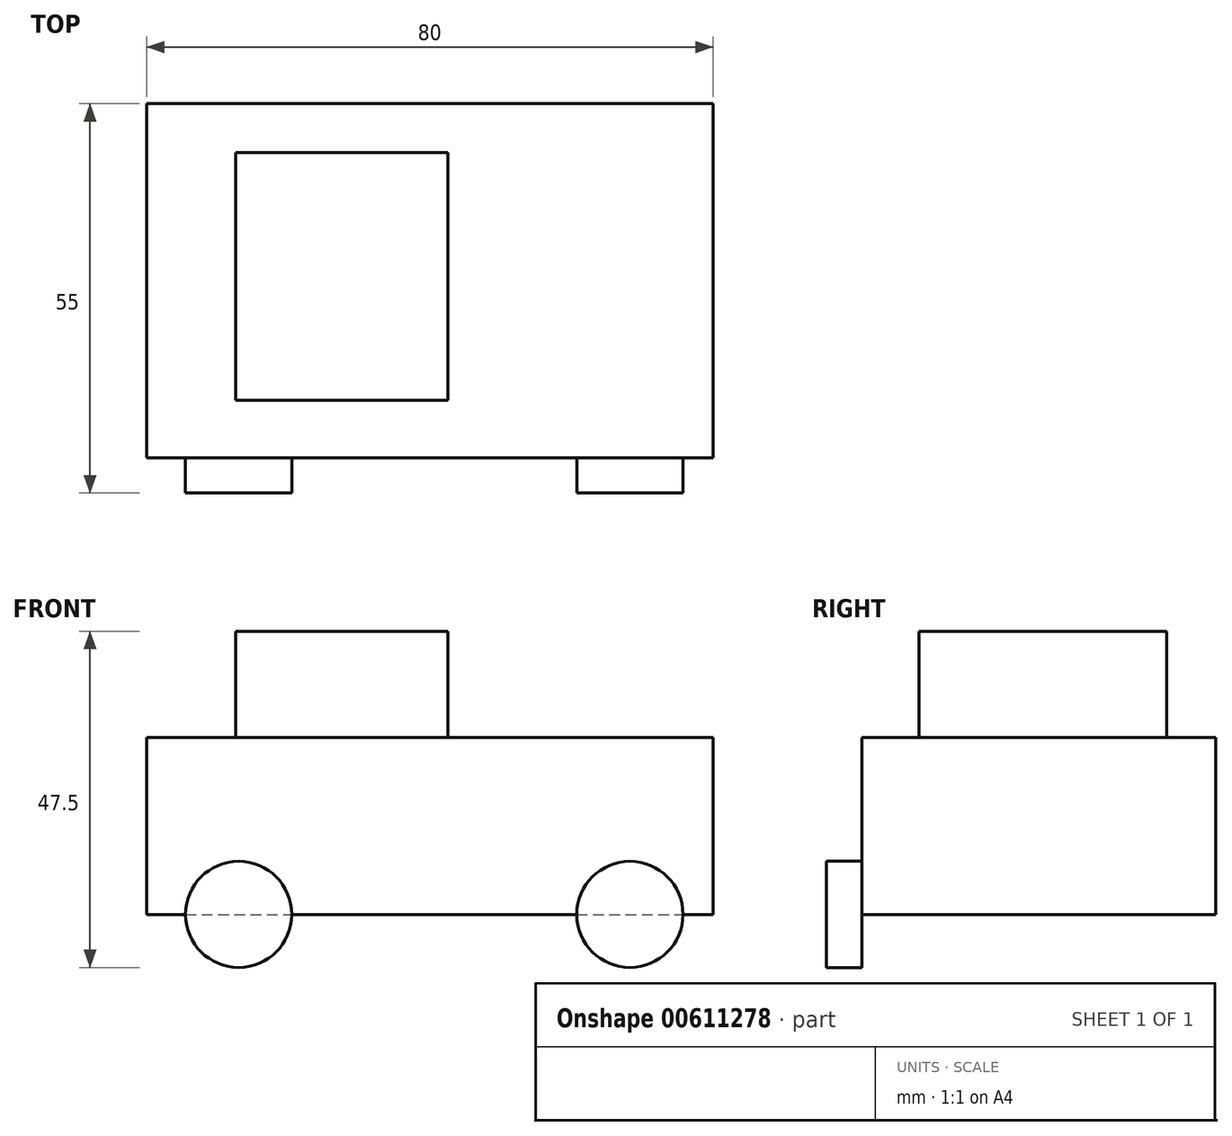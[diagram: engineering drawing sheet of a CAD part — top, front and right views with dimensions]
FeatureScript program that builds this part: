
annotation { "Feature Type Name" : "Feature", "Feature Type Description" : "" }
export const myFeature = defineFeature(function(context is Context, id is Id, definition is map)
    precondition{}
    {
        {
            var Q0;
            Q0=qCreatedBy(makeId("Top.planeOp"),FACE);
            var sketch = newSketch(context, id + "F0", { "sketchPlane" : qUnion([Q0])});
            skLineSegment(sketch, "E0.bottom", {"start": v(-39.37, 0) * mm, "end": v(40.63, 0) * mm});
            skLineSegment(sketch, "E0.top", {"start": v(-39.37, -50) * mm, "end": v(40.63, -50) * mm});
            skLineSegment(sketch, "E0.left", {"start": v(-39.37, 0) * mm, "end": v(-39.37, -50) * mm});
            skLineSegment(sketch, "E0.right", {"start": v(40.63, 0) * mm, "end": v(40.63, -50) * mm});
            skSolve(sketch);
        }
        {
            var Q0;
            Q0=makeQuery(id+"F0.imprint","IMPRINT",FACE,{"disambiguationData":[TD([[makeQuery(id+"F0.imprint","IMPRINT",EDGE,{"derivedFrom":sQuery(id+"F0.wireOp",EDGE,"E0.bottom")}),-1.0]])]});
            extrude(context, id + "F1", {"entities" : qUnion([Q0]), "depth" : 25 * mm, "offsetDistance" : 25 * mm});
        }
        {
            var Q0;
            Q0=makeQuery(id+"F1.opExtrude","CAP_FACE",FACE,{"disambiguationData":[OSD([sQuery(id+"F0.wireOp",EDGE,"E0.bottom"),sQuery(id+"F0.wireOp",EDGE,"E0.top"),sQuery(id+"F0.wireOp",EDGE,"E0.left"),sQuery(id+"F0.wireOp",EDGE,"E0.right")])],"isStart":false});
            var sketch = newSketch(context, id + "F2", { "sketchPlane" : qUnion([Q0])});
            skLineSegment(sketch, "E1.bottom", {"start": v(-26.8, -41.9) * mm, "end": v(3.2, -41.9) * mm});
            skLineSegment(sketch, "E1.top", {"start": v(-26.8, -6.9) * mm, "end": v(3.2, -6.9) * mm});
            skLineSegment(sketch, "E1.left", {"start": v(-26.8, -41.9) * mm, "end": v(-26.8, -6.9) * mm});
            skLineSegment(sketch, "E1.right", {"start": v(3.2, -41.9) * mm, "end": v(3.2, -6.9) * mm});
            skSolve(sketch);
        }
        {
            var Q0;
            Q0=makeQuery(id+"F2.imprint","IMPRINT",FACE,{"disambiguationData":[TD([[makeQuery(id+"F2.imprint","IMPRINT",EDGE,{"derivedFrom":sQuery(id+"F2.wireOp",EDGE,"E1.bottom")}),1.0]])]});
            extrude(context, id + "F3", {"entities" : qUnion([Q0]), "operationType" : NewBodyOperationType.ADD, "depth" : 15 * mm, "offsetDistance" : 25 * mm});
        }
        {
            var Q0;
            Q0=makeQuery(id+"F1.opExtrude","SWEPT_FACE",FACE,{"disambiguationData":[OSD([sQuery(id+"F0.wireOp",EDGE,"E0.top")])]});
            var sketch = newSketch(context, id + "F4", { "sketchPlane" : qUnion([Q0])});
            skCircle(sketch, "E2", {"center": v(-26.38, 0) * mm, "radius": 7.5 * mm});
            skCircle(sketch, "E3", {"center": v(28.88, 0) * mm, "radius": 7.5 * mm});
            skSolve(sketch);
        }
        {
            var Q0;
            {var subQ0=sQuery(id+"F4.wireOp",EDGE,"E2");var subQ1=makeQuery(id+"F1.opExtrude","CAP_EDGE",EDGE,{"disambiguationData":[OSD([sQuery(id+"F0.wireOp",EDGE,"E0.top")])],"isStart":true});var subQ2=makeQuery(id+"F4.imprint","INTERSECT",VERTEX,{"disambiguationData":[OD(0.0)],"derivedFrom":[subQ1,subQ0]});Q0=makeQuery(id+"F4.imprint","IMPRINT",FACE,{"disambiguationData":[TD([[makeQuery(id+"F4.imprint","IMPRINT",EDGE,{"disambiguationData":[TD([[subQ2,-1.0]])],"derivedFrom":subQ0}),1.0]])]});}
            var Q1;
            {var subQ0=sQuery(id+"F4.wireOp",EDGE,"E3");var subQ1=makeQuery(id+"F1.opExtrude","CAP_EDGE",EDGE,{"disambiguationData":[OSD([sQuery(id+"F0.wireOp",EDGE,"E0.top")])],"isStart":true});var subQ2=makeQuery(id+"F4.imprint","INTERSECT",VERTEX,{"disambiguationData":[OD(0.0)],"derivedFrom":[subQ1,subQ0]});Q1=makeQuery(id+"F4.imprint","IMPRINT",FACE,{"disambiguationData":[TD([[makeQuery(id+"F4.imprint","IMPRINT",EDGE,{"disambiguationData":[TD([[subQ2,1.0]])],"derivedFrom":subQ0}),1.0]])]});}
            var Q2;
            {var subQ0=sQuery(id+"F4.wireOp",EDGE,"E2");var subQ1=makeQuery(id+"F1.opExtrude","CAP_EDGE",EDGE,{"disambiguationData":[OSD([sQuery(id+"F0.wireOp",EDGE,"E0.top")])],"isStart":true});var subQ2=makeQuery(id+"F4.imprint","INTERSECT",VERTEX,{"disambiguationData":[OD(0.0)],"derivedFrom":[subQ1,subQ0]});Q2=makeQuery(id+"F4.imprint","IMPRINT",FACE,{"disambiguationData":[TD([[makeQuery(id+"F4.imprint","IMPRINT",EDGE,{"disambiguationData":[TD([[subQ2,1.0]])],"derivedFrom":subQ0}),1.0]])]});}
            var Q3;
            {var subQ0=sQuery(id+"F4.wireOp",EDGE,"E3");var subQ1=makeQuery(id+"F1.opExtrude","CAP_EDGE",EDGE,{"disambiguationData":[OSD([sQuery(id+"F0.wireOp",EDGE,"E0.top")])],"isStart":true});var subQ2=makeQuery(id+"F4.imprint","INTERSECT",VERTEX,{"disambiguationData":[OD(0.0)],"derivedFrom":[subQ1,subQ0]});Q3=makeQuery(id+"F4.imprint","IMPRINT",FACE,{"disambiguationData":[TD([[makeQuery(id+"F4.imprint","IMPRINT",EDGE,{"disambiguationData":[TD([[subQ2,-1.0]])],"derivedFrom":subQ0}),1.0]])]});}
            var Q4;
            Q4=sQuery(id+"F4.wireOp",EDGE,"E3");
            var Q5;
            Q5=sQuery(id+"F4.wireOp",EDGE,"E2");
            extrude(context, id + "F5", {"entities" : qUnion([Q0, Q1, Q2, Q3]), "operationType" : NewBodyOperationType.ADD, "surfaceEntities" : qUnion([Q4, Q5]), "depth" : 5 * mm, "offsetDistance" : 25 * mm});
        }
    });
